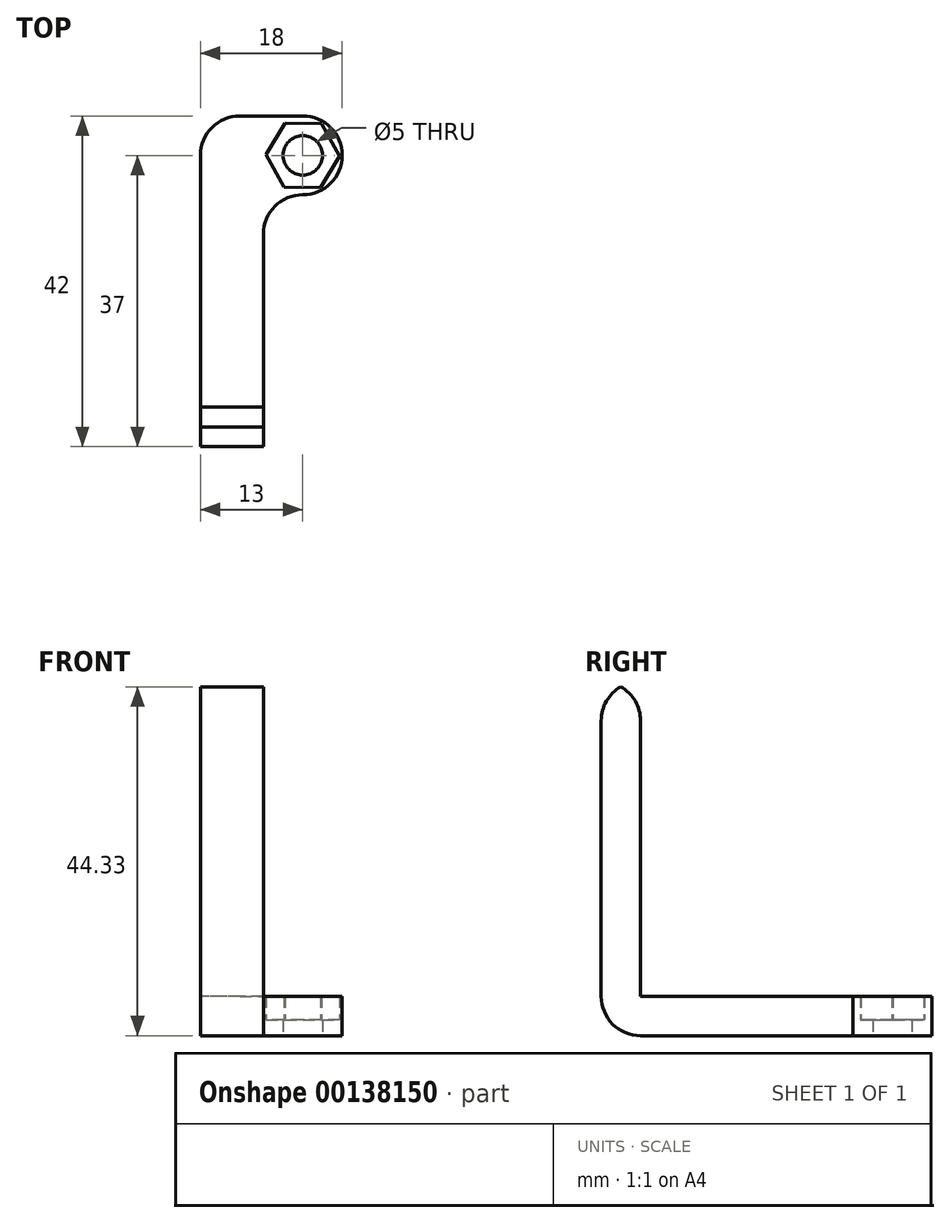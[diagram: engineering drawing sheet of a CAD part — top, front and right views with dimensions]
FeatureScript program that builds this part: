
annotation { "Feature Type Name" : "Feature", "Feature Type Description" : "" }
export const myFeature = defineFeature(function(context is Context, id is Id, definition is map)
    precondition{}
    {
        {
            var Q0;
            Q0=qCreatedBy(makeId("Top.planeOp"),FACE);
            var sketch = newSketch(context, id + "F0", { "sketchPlane" : qUnion([Q0])});
            skLineSegment(sketch, "E0.bottom", {"start": v(-9, 18.5) * mm, "end": v(9, 18.5) * mm});
            skLineSegment(sketch, "E0.left", {"start": v(-9, 18.5) * mm, "end": v(-9, -18.5) * mm});
            skPoint(sketch, "E0.middle", {"position": v(0, 0) * mm});
            skPoint(sketch, "E1", {"position": v(-9, 8.5) * mm});
            skPoint(sketch, "E2", {"position": v(-1, 18.5) * mm});
            skPoint(sketch, "E3", {"position": v(-1, 8.5) * mm});
            skPoint(sketch, "E4", {"position": v(-1, -18.5) * mm});
            skLineSegment(sketch, "E5", {"start": v(-1, 8.5) * mm, "end": v(-1, -18.5) * mm});
            skPoint(sketch, "E6", {"position": v(9, 8.5) * mm});
            skLineSegment(sketch, "E7", {"start": v(-1, 8.5) * mm, "end": v(9, 8.5) * mm});
            skLineSegment(sketch, "E8", {"start": v(9, 18.5) * mm, "end": v(9, 8.5) * mm});
            skLineSegment(sketch, "E9", {"start": v(-1, -18.5) * mm, "end": v(-9, -18.5) * mm});
            skPoint(sketch, "E10", {"position": v(4, 13.5) * mm});
            skCircle(sketch, "E11", {"center": v(4, 13.5) * mm, "radius": 2.5 * mm});
            skCircle(sketch, "E12.cCircle", {"center": v(4, 13.5) * mm, "radius": 4.05 * mm, "construction": true});
            skLineSegment(sketch, "E12.0", {"start": v(-0.68, 13.57) * mm, "end": v(1.72, 17.59) * mm});
            skLineSegment(sketch, "E12.1", {"start": v(1.72, 17.59) * mm, "end": v(6.4, 17.52) * mm});
            skLineSegment(sketch, "E12.2", {"start": v(6.4, 17.52) * mm, "end": v(8.68, 13.43) * mm});
            skLineSegment(sketch, "E12.3", {"start": v(8.68, 13.43) * mm, "end": v(6.28, 9.41) * mm});
            skLineSegment(sketch, "E12.4", {"start": v(6.28, 9.41) * mm, "end": v(1.6, 9.48) * mm});
            skLineSegment(sketch, "E12.5", {"start": v(1.6, 9.48) * mm, "end": v(-0.68, 13.57) * mm});
            skPoint(sketch, "E12.0.midPoint", {"position": v(0.52, 15.58) * mm});
            skLineSegment(sketch, "E13.top", {"start": v(-1, -23.5) * mm, "end": v(-9, -23.5) * mm});
            skLineSegment(sketch, "E13.left", {"start": v(-1, -18.5) * mm, "end": v(-1, -23.5) * mm});
            skLineSegment(sketch, "E13.right", {"start": v(-9, -18.5) * mm, "end": v(-9, -23.5) * mm});
            skSolve(sketch);
        }
        {
            var Q0;
            Q0=makeQuery(id+"F0.imprint","IMPRINT",FACE,{"disambiguationData":[TD([[makeQuery(id+"F0.imprint","IMPRINT",EDGE,{"derivedFrom":sQuery(id+"F0.wireOp",EDGE,"E9")}),1.0]])]});
            extrude(context, id + "F1", {"entities" : qUnion([Q0]), "depth" : 45 * mm});
        }
        {
            var Q0;
            Q0=makeQuery(id+"F0.imprint","IMPRINT",FACE,{"disambiguationData":[TD([[makeQuery(id+"F0.imprint","IMPRINT",EDGE,{"derivedFrom":sQuery(id+"F0.wireOp",EDGE,"E0.bottom")}),-1.0]])]});
            var Q1;
            Q1=makeQuery(id+"F0.imprint","IMPRINT",FACE,{"disambiguationData":[TD([[makeQuery(id+"F0.imprint","IMPRINT",EDGE,{"derivedFrom":sQuery(id+"F0.wireOp",EDGE,"E11")}),-1.0]])]});
            extrude(context, id + "F2", {"entities" : qUnion([Q0, Q1]), "operationType" : NewBodyOperationType.ADD, "depth" : 5 * mm});
        }
        {
            var Q0;
            Q0=makeQuery(id+"F0.imprint","IMPRINT",FACE,{"disambiguationData":[TD([[makeQuery(id+"F0.imprint","IMPRINT",EDGE,{"derivedFrom":sQuery(id+"F0.wireOp",EDGE,"E11")}),-1.0]])]});
            extrude(context, id + "F3", {"entities" : qUnion([Q0]), "operationType" : NewBodyOperationType.REMOVE, "depth" : 10 * mm});
        }
        {
            var Q0;
            Q0=makeQuery(id+"F0.imprint","IMPRINT",FACE,{"disambiguationData":[TD([[makeQuery(id+"F0.imprint","IMPRINT",EDGE,{"derivedFrom":sQuery(id+"F0.wireOp",EDGE,"E11")}),-1.0]])]});
            extrude(context, id + "F4", {"entities" : qUnion([Q0]), "operationType" : NewBodyOperationType.ADD, "depth" : 2 * mm});
        }
        {
            var Q0;
            Q0=makeQuery(id+"F2.opExtrude","SWEPT_EDGE",EDGE,{"disambiguationData":[OSD([sQuery(id+"F0.wireOp",EDGE,"E5"),sQuery(id+"F0.wireOp",EDGE,"E7")])]});
            var Q1;
            Q1=makeQuery(id+"F2.opExtrude","SWEPT_EDGE",EDGE,{"disambiguationData":[OSD([sQuery(id+"F0.wireOp",EDGE,"E0.bottom"),sQuery(id+"F0.wireOp",EDGE,"E0.left")])]});
            var Q2;
            Q2=makeQuery(id+"F2.opExtrude","SWEPT_EDGE",EDGE,{"disambiguationData":[OSD([sQuery(id+"F0.wireOp",EDGE,"E0.bottom"),sQuery(id+"F0.wireOp",EDGE,"E8")])]});
            var Q3;
            Q3=makeQuery(id+"F2.opExtrude","SWEPT_EDGE",EDGE,{"disambiguationData":[OSD([sQuery(id+"F0.wireOp",EDGE,"E7"),sQuery(id+"F0.wireOp",EDGE,"E8")])]});
            var Q4;
            Q4=makeQuery(id+"F1.opExtrude","CAP_EDGE",EDGE,{"disambiguationData":[OSD([sQuery(id+"F0.wireOp",EDGE,"E13.top")])],"isStart":true});
            var Q5;
            Q5=makeQuery(id+"F1.opExtrude","CAP_EDGE",EDGE,{"disambiguationData":[OSD([sQuery(id+"F0.wireOp",EDGE,"E13.top")])],"isStart":false});
            var Q6;
            Q6=makeQuery(id+"F1.opExtrude","CAP_EDGE",EDGE,{"disambiguationData":[OSD([sQuery(id+"F0.wireOp",EDGE,"E9")])],"isStart":false});
            fillet(context, id + "F5", {"entities" : qUnion([Q0, Q1, Q2, Q3, Q4, Q5, Q6]), "radius" : 5 * mm, "tangentPropagation" : true, "allowEdgeOverflow" : false});
        }
    });
